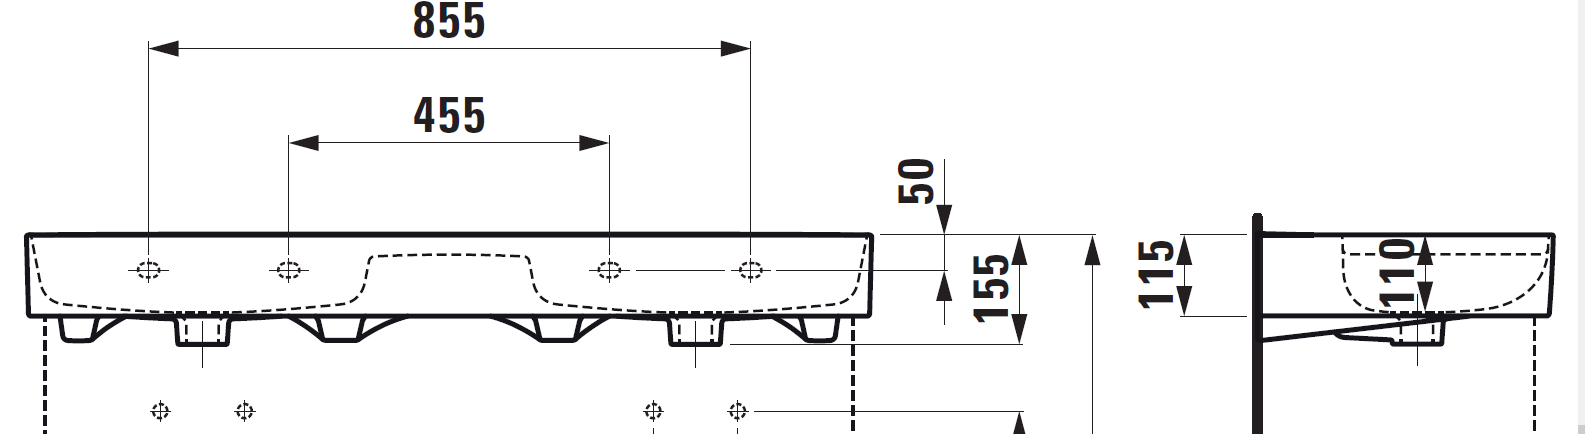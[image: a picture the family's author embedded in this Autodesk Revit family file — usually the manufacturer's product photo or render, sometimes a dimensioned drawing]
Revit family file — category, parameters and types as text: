
# Revit family: Reece_Basin_LAUFEN_Val_Double Wall Basin_1200 mm x 420 mm
name_source: partatom
category: Plumbing Fixtures
revit_build: Autodesk Revit 2018 (Build: 20190510_1515(x64)
units: mm (PartAtom-declared; Revit-internal decimal feet)

## family parameters
Cut with Voids When Loaded = Yes
Host = Face
Part Type = Normal
Room Calculation Point = Yes
Round Connector Dimension = Use Diameter
Shared = Yes

## types (1)
- 1200 mm_2 Taphole_SaphirKeramik_White_With Fixing
    Default Elevation = 0 mm  [stored 0 ft]
    Description = LAUFEN Val Double Wall Basin 2 Taphole with Overflow 1200x420 Internal Texture with Fixing Bolts White
    Disclaimer = THIS FILE IS THE PROPERTY OF THE REECE GROUP. IT MAY NOT BE REPRODUCED, REVERSE-ENGINEERED OR MODIFIED. ANY REPUBLICATION, TRANSMISSION OR DISTRIBUTION FOR THE PURPOSE OF COMMERCIALLY EXPLOITING THE FILES IS PROHIBITED.
    Keynote = Product #1810958, Reece_Basin_LAUFEN_Val_Double Wall Basin_1200 mm x 420 mm - 1200 mm_2 Taphole_SaphirKeramik_White_With Fixing
    Manufacturer = LAUFEN
    Model = Val
    Reece_Basin_Outlet = 40 mm  [stored 0.131234 ft]
    Reece_Detail_Additional = With Fixing, Internal Texture, Overflow
    Reece_Detail_Connector = 2 Taphole
    Reece_Detail_Disclaimer = THIS FILE IS THE PROPERTY OF THE REECE GROUP. IT MAY NOT BE REPRODUCED, REVERSE-ENGINEERED OR MODIFIED. ANY REPUBLICATION, TRANSMISSION OR DISTRIBUTION FOR THE PURPOSE OF COMMERCIALLY EXPLOITING THE FILES IS PROHIBITED.
    Reece_Detail_Installation = Double Wall Basin
    Reece_Detail_Shape = Left & Right Hand Bowls
    Reece_Material_Main = Reece_SaphirKeramik_White
    Reece_Material_Secondary = Reece_Brass_Chrome
    Reece_Overall_Capacity = 8.6 L
    Reece_Overall_Depth = 420 mm  [stored 1.37795 ft]
    Reece_Overall_Height = 155 mm  [stored 0.50853 ft]
    Reece_Overall_Width = 1200 mm
    Reece_Product_Brand = LAUFEN
    Reece_Product_Description = LAUFEN Val Double Wall Basin 2 Taphole with Overflow 1200x420 Internal Texture with Fixing Bolts White
    Reece_Product_Mount = Wall Mounted
    Reece_Product_Number = 1810958
    Reece_Product_Sub Brand = Val
    Reece_Product_Type = Basin
    Reece_Product_Web Page = https://www.reece.com.au
    Type Comments = Basin
    URL = https://www.reece.com.au

note: [stored X ft] marks values corroborated as IEEE doubles in the binary element streams (Revit-internal decimal feet)

## geometry (parser evidence)
native form markers: Sweep x6
no freeform markers — native parametric forms only
